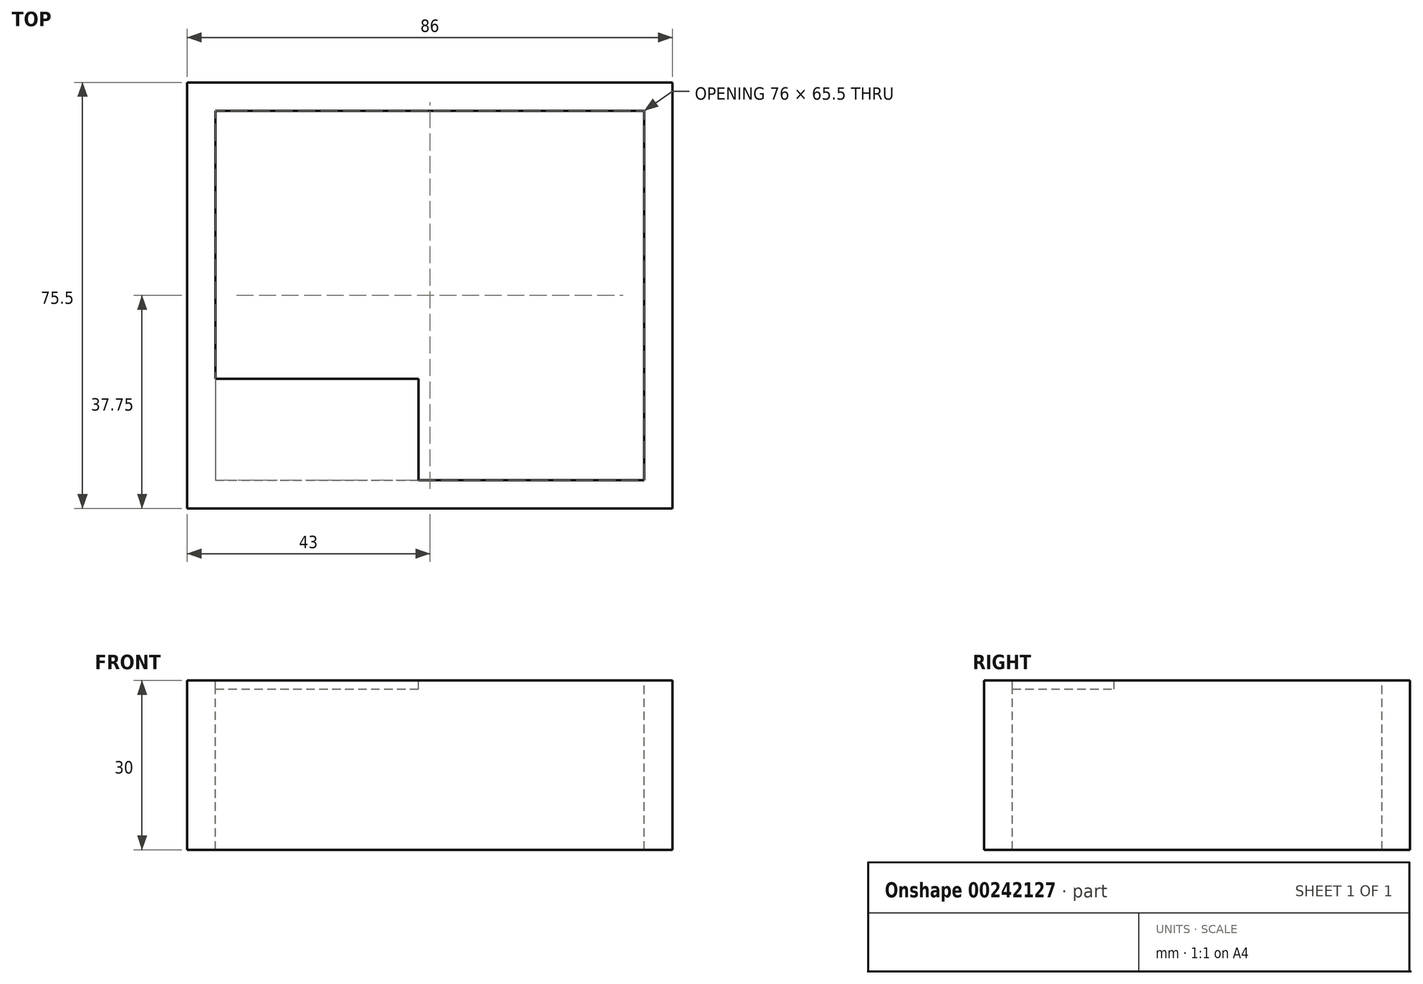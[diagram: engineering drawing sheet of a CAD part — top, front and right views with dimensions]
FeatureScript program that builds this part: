
annotation { "Feature Type Name" : "Feature", "Feature Type Description" : "" }
export const myFeature = defineFeature(function(context is Context, id is Id, definition is map)
    precondition{}
    {
        {
            var Q0;
            Q0=qCreatedBy(makeId("Top.planeOp"),FACE);
            var sketch = newSketch(context, id + "F0", { "sketchPlane" : qUnion([Q0])});
            skLineSegment(sketch, "E0.bottom", {"start": v(43, 37.75) * mm, "end": v(-43, 37.75) * mm});
            skLineSegment(sketch, "E0.top", {"start": v(43, -37.75) * mm, "end": v(-43, -37.75) * mm});
            skLineSegment(sketch, "E0.left", {"start": v(43, 37.75) * mm, "end": v(43, -37.75) * mm});
            skLineSegment(sketch, "E0.right", {"start": v(-43, 37.75) * mm, "end": v(-43, -37.75) * mm});
            skPoint(sketch, "E0.middle", {"position": v(0, 0) * mm});
            skLineSegment(sketch, "E1.bottom", {"start": v(-38, 32.75) * mm, "end": v(38, 32.75) * mm});
            skLineSegment(sketch, "E1.top", {"start": v(-38, -32.75) * mm, "end": v(38, -32.75) * mm});
            skLineSegment(sketch, "E1.left", {"start": v(-38, 32.75) * mm, "end": v(-38, -32.75) * mm});
            skLineSegment(sketch, "E1.right", {"start": v(38, 32.75) * mm, "end": v(38, -32.75) * mm});
            skLineSegment(sketch, "E2.bottom", {"start": v(-29, 32.75) * mm, "end": v(29, 32.75) * mm});
            skLineSegment(sketch, "E2.top", {"start": v(-29, -5.25) * mm, "end": v(29, -5.25) * mm});
            skLineSegment(sketch, "E2.left", {"start": v(-29, 27.75) * mm, "end": v(-29, -5.25) * mm});
            skLineSegment(sketch, "E2.right", {"start": v(29, 27.75) * mm, "end": v(29, -5.25) * mm});
            skCircle(sketch, "E3", {"center": v(29, -23.05) * mm, "radius": 8 * mm});
            skLineSegment(sketch, "E4.bottom", {"start": v(-38, -32.75) * mm, "end": v(-2, -32.75) * mm});
            skLineSegment(sketch, "E4.top", {"start": v(-38, -14.75) * mm, "end": v(-2, -14.75) * mm});
            skLineSegment(sketch, "E4.left", {"start": v(-38, -32.75) * mm, "end": v(-38, -14.75) * mm});
            skLineSegment(sketch, "E4.right", {"start": v(-2, -32.75) * mm, "end": v(-2, -14.75) * mm});
            skLineSegment(sketch, "E5", {"start": v(-29, 27.75) * mm, "end": v(29, 27.75) * mm});
            skSolve(sketch);
        }
        {
            var Q0;
            Q0=makeQuery(id+"F0.imprint","IMPRINT",FACE,{"disambiguationData":[TD([[makeQuery(id+"F0.imprint","IMPRINT",EDGE,{"derivedFrom":sQuery(id+"F0.wireOp",EDGE,"E1.top")}),1.0]])]});
            extrude(context, id + "F1", {"entities" : qUnion([Q0]), "oppositeDirection" : true, "depth" : 1.5 * mm});
        }
        {
            var Q0;
            Q0 = qSketchRegion(id + "F0", true);
            extrude(context, id + "F2", {"entities" : qUnion([Q0]), "operationType" : NewBodyOperationType.ADD, "oppositeDirection" : true, "depth" : 30 * mm});
        }
    });
